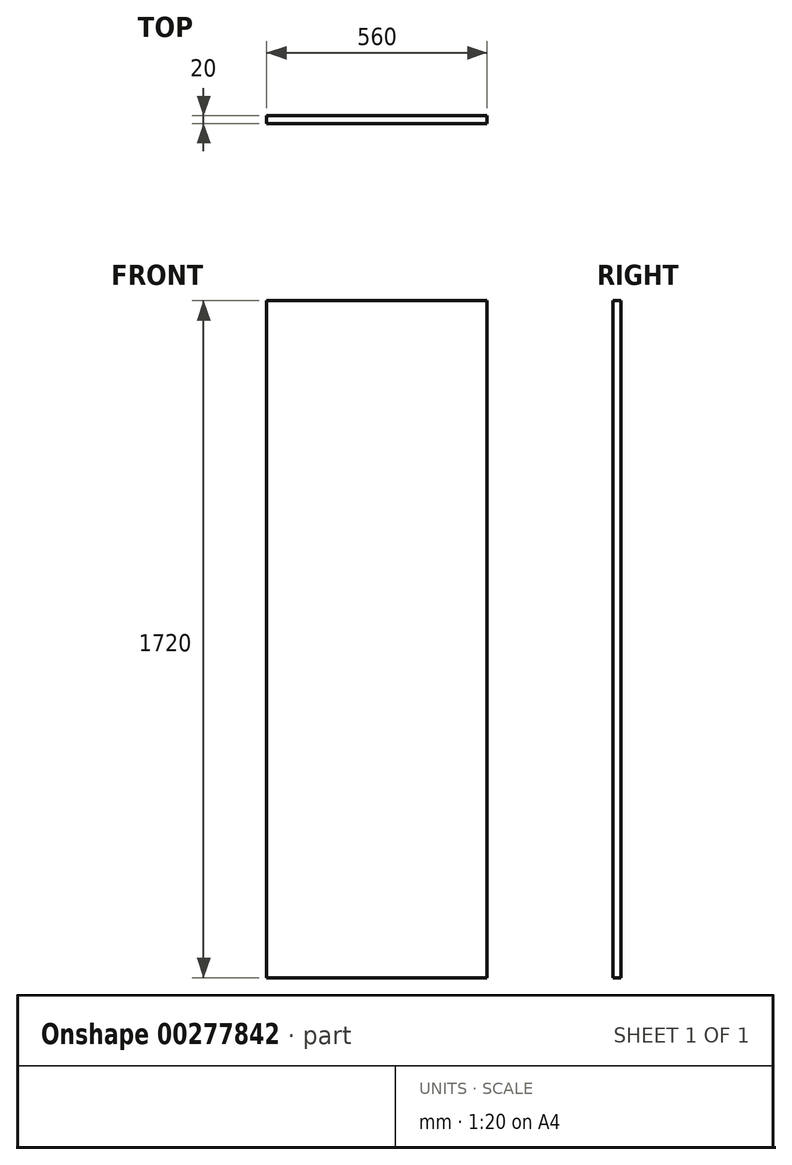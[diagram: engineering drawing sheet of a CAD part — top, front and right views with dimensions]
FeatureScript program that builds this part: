
annotation { "Feature Type Name" : "Feature", "Feature Type Description" : "" }
export const myFeature = defineFeature(function(context is Context, id is Id, definition is map)
    precondition{}
    {
        {
            var Q0;
            Q0=qCreatedBy(makeId("Front.planeOp"),FACE);
            var sketch = newSketch(context, id + "F0", { "sketchPlane" : qUnion([Q0])});
            skLineSegment(sketch, "E0.bottom", {"start": v(-560, -1720) * mm, "end": v(0, -1720) * mm});
            skLineSegment(sketch, "E0.top", {"start": v(-560, 0) * mm, "end": v(0, 0) * mm});
            skLineSegment(sketch, "E0.left", {"start": v(-560, -1720) * mm, "end": v(-560, 0) * mm});
            skLineSegment(sketch, "E0.right", {"start": v(0, -1720) * mm, "end": v(0, 0) * mm});
            skSolve(sketch);
        }
        {
            var Q0;
            Q0 = qSketchRegion(id + "F0", true);
            extrude(context, id + "F1", {"entities" : qUnion([Q0]), "depth" : 20 * mm});
        }
    });
